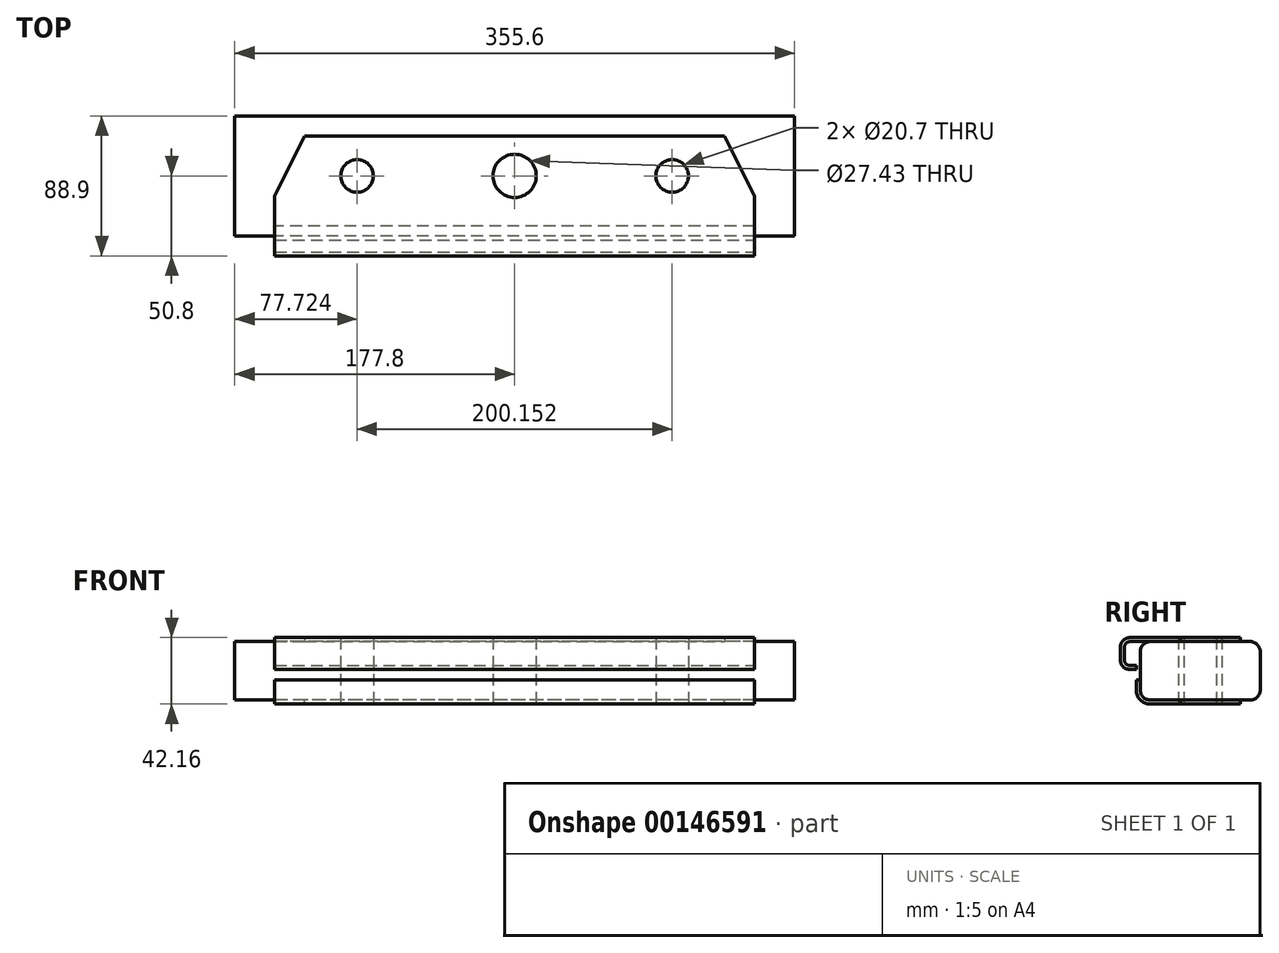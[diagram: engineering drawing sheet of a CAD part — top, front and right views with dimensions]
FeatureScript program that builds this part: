
annotation { "Feature Type Name" : "Feature", "Feature Type Description" : "" }
export const myFeature = defineFeature(function(context is Context, id is Id, definition is map)
    precondition{}
    {
        {
            var Q0;
            Q0=qCreatedBy(makeId("Top.planeOp"),FACE);
            var sketch = newSketch(context, id + "F0", { "sketchPlane" : qUnion([Q0])});
            skLineSegment(sketch, "E0.bottom", {"start": v(177.8, 38.1) * mm, "end": v(-177.8, 38.1) * mm});
            skLineSegment(sketch, "E0.top", {"start": v(177.8, -38.1) * mm, "end": v(-177.8, -38.1) * mm});
            skLineSegment(sketch, "E0.left", {"start": v(177.8, 38.1) * mm, "end": v(177.8, -38.1) * mm});
            skLineSegment(sketch, "E0.right", {"start": v(-177.8, 38.1) * mm, "end": v(-177.8, -38.1) * mm});
            skPoint(sketch, "E0.middle", {"position": v(0, 0) * mm});
            skCircle(sketch, "E1", {"center": v(0, 0) * mm, "radius": 13.72 * mm});
            skLineSegment(sketch, "E2", {"start": v(13.72, 0) * mm, "end": v(100.08, 0) * mm, "construction": true});
            skLineSegment(sketch, "E3", {"start": v(-13.72, 0) * mm, "end": v(-100.08, 0) * mm, "construction": true});
            skCircle(sketch, "E4", {"center": v(-100.08, 0) * mm, "radius": 10.35 * mm});
            skCircle(sketch, "E5", {"center": v(100.08, 0) * mm, "radius": 10.35 * mm});
            skSolve(sketch);
        }
        {
            var Q0;
            Q0=makeQuery(id+"F0.imprint","IMPRINT",FACE,{"disambiguationData":[TD([[makeQuery(id+"F0.imprint","IMPRINT",EDGE,{"derivedFrom":sQuery(id+"F0.wireOp",EDGE,"E0.bottom")}),1.0]])]});
            extrude(context, id + "F1", {"entities" : qUnion([Q0]), "depth" : 37.08 * mm});
        }
        {
            var Q0;
            Q0=makeQuery(id+"F1.opExtrude","CAP_EDGE",EDGE,{"disambiguationData":[OSD([sQuery(id+"F0.wireOp",EDGE,"E0.top")])],"isStart":false});
            var Q1;
            Q1=makeQuery(id+"F1.opExtrude","CAP_EDGE",EDGE,{"disambiguationData":[OSD([sQuery(id+"F0.wireOp",EDGE,"E0.top")])],"isStart":true});
            var Q2;
            Q2=makeQuery(id+"F1.opExtrude","CAP_EDGE",EDGE,{"disambiguationData":[OSD([sQuery(id+"F0.wireOp",EDGE,"E0.bottom")])],"isStart":false});
            var Q3;
            Q3=makeQuery(id+"F1.opExtrude","CAP_EDGE",EDGE,{"disambiguationData":[OSD([sQuery(id+"F0.wireOp",EDGE,"E0.bottom")])],"isStart":true});
            fillet(context, id + "F2", {"entities" : qUnion([Q0, Q1, Q2, Q3]), "radius" : 6.35 * mm, "tangentPropagation" : true, "allowEdgeOverflow" : false});
        }
        {
            var Q0;
            Q0=makeQuery(id+"F1.opExtrude","CAP_FACE",FACE,{"disambiguationData":[OSD([sQuery(id+"F0.wireOp",EDGE,"E0.bottom"),sQuery(id+"F0.wireOp",EDGE,"E0.top"),sQuery(id+"F0.wireOp",EDGE,"E0.left"),sQuery(id+"F0.wireOp",EDGE,"E0.right"),sQuery(id+"F0.wireOp",EDGE,"E1"),sQuery(id+"F0.wireOp",EDGE,"E4"),sQuery(id+"F0.wireOp",EDGE,"E5")])],"isStart":false});
            var sketch = newSketch(context, id + "F3", { "sketchPlane" : qUnion([Q0])});
            skLineSegment(sketch, "E6.bottom", {"start": v(-152.4, -44.45) * mm, "end": v(152.4, -44.45) * mm});
            skLineSegment(sketch, "E6.top", {"start": v(-133.35, 25.4) * mm, "end": v(133.35, 25.4) * mm});
            skLineSegment(sketch, "E6.left", {"start": v(-152.4, -44.45) * mm, "end": v(-152.4, -12.7) * mm});
            skLineSegment(sketch, "E6.right", {"start": v(152.4, -44.45) * mm, "end": v(152.4, -12.7) * mm});
            skLineSegment(sketch, "E7", {"start": v(-152.4, -12.7) * mm, "end": v(-133.35, 25.4) * mm});
            skLineSegment(sketch, "E8", {"start": v(152.4, -12.7) * mm, "end": v(133.35, 25.4) * mm});
            skSolve(sketch);
        }
        {
            var Q0;
            {var subQ0=sQuery(id+"F3.wireOp",EDGE,"E6.bottom");Q0=makeQuery(id+"F3.imprint","IMPRINT",FACE,{"disambiguationData":[TD([[makeQuery(id+"F3.imprint","IMPRINT",EDGE,{"derivedFrom":subQ0}),1.0]])]});}
            var Q1;
            {var subQ1=sQuery(id+"F3.wireOp",EDGE,"E6.top");Q1=makeQuery(id+"F3.imprint","IMPRINT",FACE,{"disambiguationData":[TD([[makeQuery(id+"F3.imprint","IMPRINT",EDGE,{"derivedFrom":subQ1}),-1.0]])]});}
            extrude(context, id + "F4", {"entities" : qUnion([Q0, Q1]), "operationType" : NewBodyOperationType.ADD, "depth" : 2.54 * mm});
        }
        {
            var Q0;
            Q0=makeQuery(id+"F1.opExtrude","CAP_FACE",FACE,{"disambiguationData":[OSD([sQuery(id+"F0.wireOp",EDGE,"E0.bottom"),sQuery(id+"F0.wireOp",EDGE,"E0.top"),sQuery(id+"F0.wireOp",EDGE,"E0.left"),sQuery(id+"F0.wireOp",EDGE,"E0.right"),sQuery(id+"F0.wireOp",EDGE,"E1"),sQuery(id+"F0.wireOp",EDGE,"E4"),sQuery(id+"F0.wireOp",EDGE,"E5")])],"isStart":true});
            var sketch = newSketch(context, id + "F5", { "sketchPlane" : qUnion([Q0])});
            skLineSegment(sketch, "E9", {"start": v(-133.35, -25.4) * mm, "end": v(-152.4, 12.7) * mm});
            skLineSegment(sketch, "E10", {"start": v(152.4, 12.7) * mm, "end": v(133.35, -25.4) * mm});
            skLineSegment(sketch, "E11", {"start": v(133.35, -25.4) * mm, "end": v(-133.35, -25.4) * mm});
            skLineSegment(sketch, "E12", {"start": v(-152.4, 12.7) * mm, "end": v(-152.4, 31.75) * mm});
            skLineSegment(sketch, "E13", {"start": v(-152.4, 31.75) * mm, "end": v(152.4, 31.75) * mm});
            skLineSegment(sketch, "E14", {"start": v(152.4, 31.75) * mm, "end": v(152.4, 12.7) * mm});
            skSolve(sketch);
        }
        {
            var Q0;
            Q0=makeQuery(id+"F5.imprint","IMPRINT",FACE,{"disambiguationData":[TD([[makeQuery(id+"F5.imprint","IMPRINT",EDGE,{"derivedFrom":sQuery(id+"F5.wireOp",EDGE,"E9")}),-1.0]])]});
            extrude(context, id + "F6", {"entities" : qUnion([Q0]), "operationType" : NewBodyOperationType.ADD, "depth" : 2.54 * mm});
        }
        {
            var Q0;
            Q0=makeQuery(id+"F4.opExtrude","SWEPT_FACE",FACE,{"disambiguationData":[OSD([sQuery(id+"F3.wireOp",EDGE,"E6.right")])]});
            var sketch = newSketch(context, id + "F7", { "sketchPlane" : qUnion([Q0])});
            skLineSegment(sketch, "E15", {"start": v(-44.45, 39.62) * mm, "end": v(-44.45, 39.62) * mm});
            skLineSegment(sketch, "E16", {"start": v(-44.45, 37.08) * mm, "end": v(-44.45, 39.62) * mm});
            skArc(sketch, "E17.MirrorCS", {"start": v(-48.26, 25.65) * mm, "mid": v(-47.14, 22.96) * mm, "end": v(-44.45, 21.84) * mm});
            skArc(sketch, "E18.MirrorCS", {"start": v(-44.45, 19.3) * mm, "mid": v(-48.94, 21.16) * mm, "end": v(-50.8, 25.65) * mm});
            skLineSegment(sketch, "E19.MirrorCS", {"start": v(-50.8, 33.27) * mm, "end": v(-50.8, 25.65) * mm});
            skLineSegment(sketch, "E20.MirrorCS", {"start": v(-48.26, 25.65) * mm, "end": v(-48.26, 33.27) * mm});
            skArc(sketch, "E21.MirrorCS", {"start": v(-44.45, 37.08) * mm, "mid": v(-47.14, 35.97) * mm, "end": v(-48.26, 33.27) * mm});
            skArc(sketch, "E22.MirrorCS", {"start": v(-50.8, 33.27) * mm, "mid": v(-48.94, 37.76) * mm, "end": v(-44.45, 39.62) * mm});
            skLineSegment(sketch, "E23.MirrorCS", {"start": v(-44.45, 19.3) * mm, "end": v(-40.64, 19.3) * mm});
            skLineSegment(sketch, "E24.MirrorCS", {"start": v(-40.64, 21.84) * mm, "end": v(-44.45, 21.84) * mm});
            skLineSegment(sketch, "E25.MirrorCS", {"start": v(-40.64, 19.3) * mm, "end": v(-40.64, 21.84) * mm});
            skSolve(sketch);
        }
        {
            var Q0;
            Q0=makeQuery(id+"F7.imprint","IMPRINT",FACE,{"disambiguationData":[TD([[makeQuery(id+"F7.imprint","IMPRINT",EDGE,{"derivedFrom":sQuery(id+"F7.wireOp",EDGE,"E16")}),-1.0]])]});
            extrude(context, id + "F8", {"entities" : qUnion([Q0]), "operationType" : NewBodyOperationType.ADD, "oppositeDirection" : true, "depth" : 304.8 * mm});
        }
        {
            var Q0;
            Q0=makeQuery(id+"F6.opExtrude","SWEPT_FACE",FACE,{"disambiguationData":[OSD([sQuery(id+"F5.wireOp",EDGE,"E12")])]});
            var sketch = newSketch(context, id + "F9", { "sketchPlane" : qUnion([Q0])});
            skLineSegment(sketch, "E26", {"start": v(31.75, 0) * mm, "end": v(31.75, 0) * mm});
            skLineSegment(sketch, "E27", {"start": v(40.64, 6.35) * mm, "end": v(40.64, 12.7) * mm});
            skLineSegment(sketch, "E28", {"start": v(40.64, 12.7) * mm, "end": v(38.1, 12.7) * mm});
            skLineSegment(sketch, "E29", {"start": v(38.1, 12.7) * mm, "end": v(38.1, 6.35) * mm});
            skArc(sketch, "E30.filletArc", {"start": v(31.75, 0) * mm, "mid": v(36.24, 1.86) * mm, "end": v(38.1, 6.35) * mm});
            skArc(sketch, "E31", {"start": v(40.64, 6.35) * mm, "mid": v(38.04, 0.06) * mm, "end": v(31.75, -2.54) * mm});
            skLineSegment(sketch, "E32", {"start": v(31.75, -2.54) * mm, "end": v(31.75, 0) * mm});
            skSolve(sketch);
        }
        {
            var Q0;
            Q0=makeQuery(id+"F9.imprint","IMPRINT",FACE,{"disambiguationData":[TD([[makeQuery(id+"F9.imprint","IMPRINT",EDGE,{"derivedFrom":sQuery(id+"F9.wireOp",EDGE,"E27")}),1.0]])]});
            extrude(context, id + "F10", {"entities" : qUnion([Q0]), "operationType" : NewBodyOperationType.ADD, "oppositeDirection" : true, "depth" : 304.8 * mm});
        }
    });
